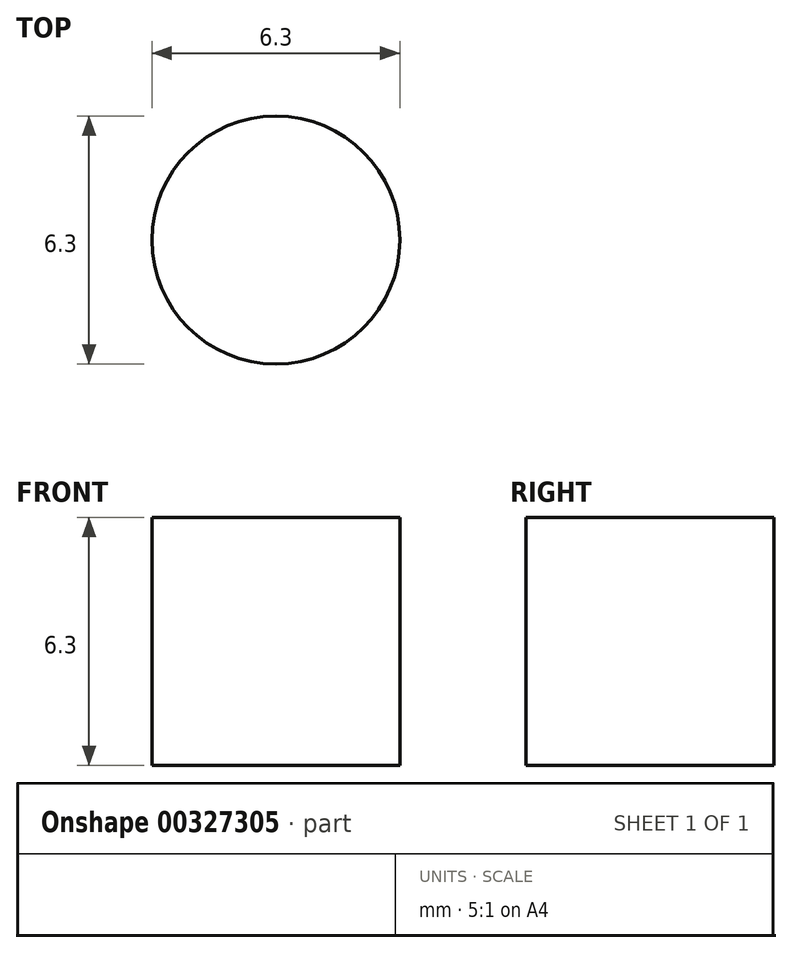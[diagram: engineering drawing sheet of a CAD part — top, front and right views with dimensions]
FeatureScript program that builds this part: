
annotation { "Feature Type Name" : "Feature", "Feature Type Description" : "" }
export const myFeature = defineFeature(function(context is Context, id is Id, definition is map)
    precondition{}
    {
        {
            var Q0;
            Q0=qCreatedBy(makeId("Top.planeOp"),FACE);
            var sketch = newSketch(context, id + "F0", { "sketchPlane" : qUnion([Q0])});
            skCircle(sketch, "E0", {"center": v(0, 0) * mm, "radius": 3.15 * mm});
            skSolve(sketch);
        }
        {
            var Q0;
            Q0 = qSketchRegion(id + "F0", true);
            extrude(context, id + "F1", {"entities" : qUnion([Q0]), "endBound" : BoundingType.SYMMETRIC, "depth" : 6.3 * mm, "offsetDistance" : 25 * mm});
        }
    });
